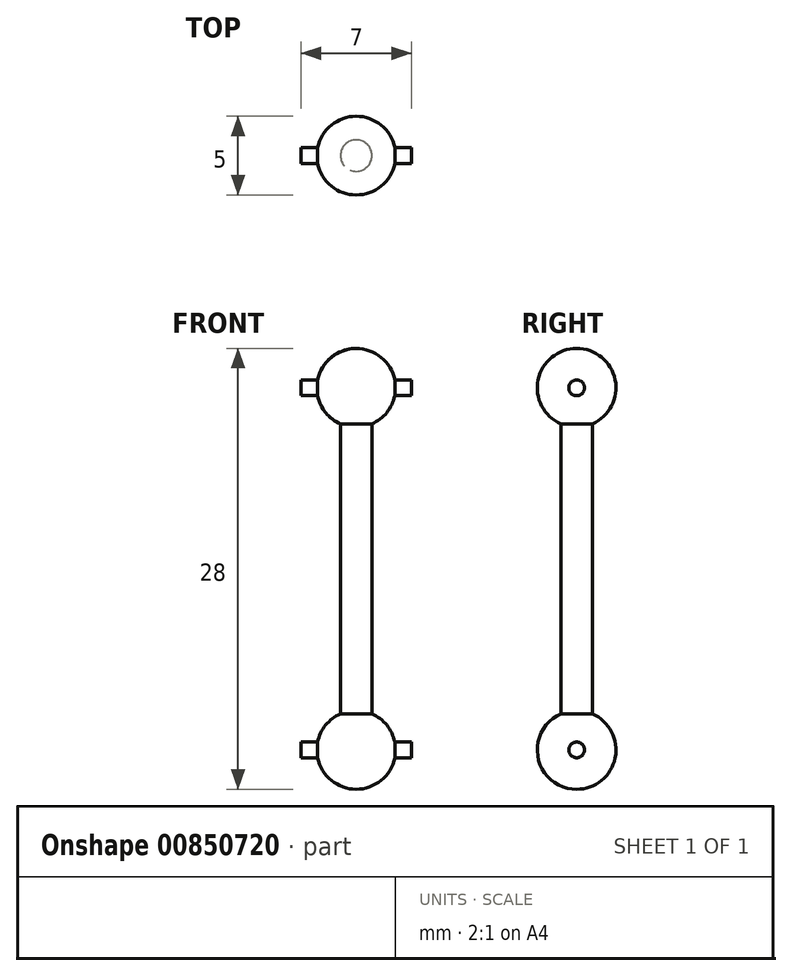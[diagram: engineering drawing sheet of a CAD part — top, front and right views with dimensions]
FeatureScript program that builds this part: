
annotation { "Feature Type Name" : "Feature", "Feature Type Description" : "" }
export const myFeature = defineFeature(function(context is Context, id is Id, definition is map)
    precondition{}
    {
        {
            assignVariable(context, id + "F0", {"name" : "Len", "anyValue" : 23});
        }
        {
            var Q0;
            Q0=qCreatedBy(makeId("Top.planeOp"),FACE);
            var sketch = newSketch(context, id + "F1", { "sketchPlane" : qUnion([Q0])});
            skCircle(sketch, "E0", {"center": v(0, 0) * mm, "radius": 1 * mm});
            skSolve(sketch);
        }
        {
            var Q0;
            Q0 = qSketchRegion(id + "F1", true);
            extrude(context, id + "F2", {"entities" : qUnion([Q0]), "depth" : (getVariable(context, 'Len')) * mm, "offsetDistance" : 25 * mm});
        }
        {
            var Q0;
            Q0=qCreatedBy(makeId("Right.planeOp"),FACE);
            var sketch = newSketch(context, id + "F3", { "sketchPlane" : qUnion([Q0])});
            skArc(sketch, "E1", {"start": v(-0.5, 2.45) * mm, "mid": v(-2.49, -0.25) * mm, "end": v(0, -2.5) * mm});
            skLineSegment(sketch, "E2", {"start": v(0, -2.5) * mm, "end": v(0, 0) * mm});
            skLineSegment(sketch, "E3", {"start": v(0, 0) * mm, "end": v(-0.5, 0) * mm});
            skLineSegment(sketch, "E4", {"start": v(-0.5, 0) * mm, "end": v(-0.5, 2.45) * mm});
            skSolve(sketch);
        }
        {
            var Q0;
            Q0=makeQuery(id+"F3.imprint","IMPRINT",FACE,{"disambiguationData":[TD([[makeQuery(id+"F3.imprint","IMPRINT",EDGE,{"derivedFrom":sQuery(id+"F3.wireOp",EDGE,"E1")}),1.0]])]});
            var Q1;
            Q1=sQuery(id+"F3.wireOp",EDGE,"E2");
            revolve(context, id + "F4", {"operationType" : NewBodyOperationType.ADD, "surfaceOperationType" : NewSurfaceOperationType.NEW, "entities" : qUnion([Q0]), "axis" : qUnion([Q1]), "revolveType" : RevolveType.FULL});
        }
        {
            var Q0;
            Q0=qCreatedBy(makeId("Front.planeOp"),FACE);
            var sketch = newSketch(context, id + "F5", { "sketchPlane" : qUnion([Q0])});
            skArc(sketch, "E5", {"start": v(0, 25.5) * mm, "mid": v(-2.45, 23.51) * mm, "end": v(-1, 20.7) * mm});
            skLineSegment(sketch, "E6", {"start": v(-1, 20.7) * mm, "end": v(-1, 23) * mm});
            skLineSegment(sketch, "E7", {"start": v(-1, 23) * mm, "end": v(0, 23) * mm});
            skLineSegment(sketch, "E8", {"start": v(0, 23) * mm, "end": v(0, 25.5) * mm});
            skSolve(sketch);
        }
        {
            var Q0;
            Q0 = qSketchRegion(id + "F5", true);
            var Q1;
            Q1=sQuery(id+"F5.wireOp",EDGE,"E8");
            revolve(context, id + "F6", {"operationType" : NewBodyOperationType.ADD, "surfaceOperationType" : NewSurfaceOperationType.NEW, "entities" : qUnion([Q0]), "axis" : qUnion([Q1]), "revolveType" : RevolveType.FULL});
        }
        {
            var Q0;
            Q0=qCreatedBy(makeId("Right.planeOp"),FACE);
            var sketch = newSketch(context, id + "F7", { "sketchPlane" : qUnion([Q0])});
            skCircle(sketch, "E9", {"center": v(0, 0) * mm, "radius": 0.5 * mm});
            skCircle(sketch, "E10", {"center": v(0, 23) * mm, "radius": 0.5 * mm});
            skSolve(sketch);
        }
        {
            var Q0;
            Q0 = qSketchRegion(id + "F7", true);
            extrude(context, id + "F8", {"entities" : qUnion([Q0]), "operationType" : NewBodyOperationType.ADD, "depth" : 3.5 * mm, "offsetDistance" : 25 * mm, "hasSecondDirection" : true, "secondDirectionOppositeDirection" : true, "secondDirectionDepth" : 3.5 * mm});
        }
    });
